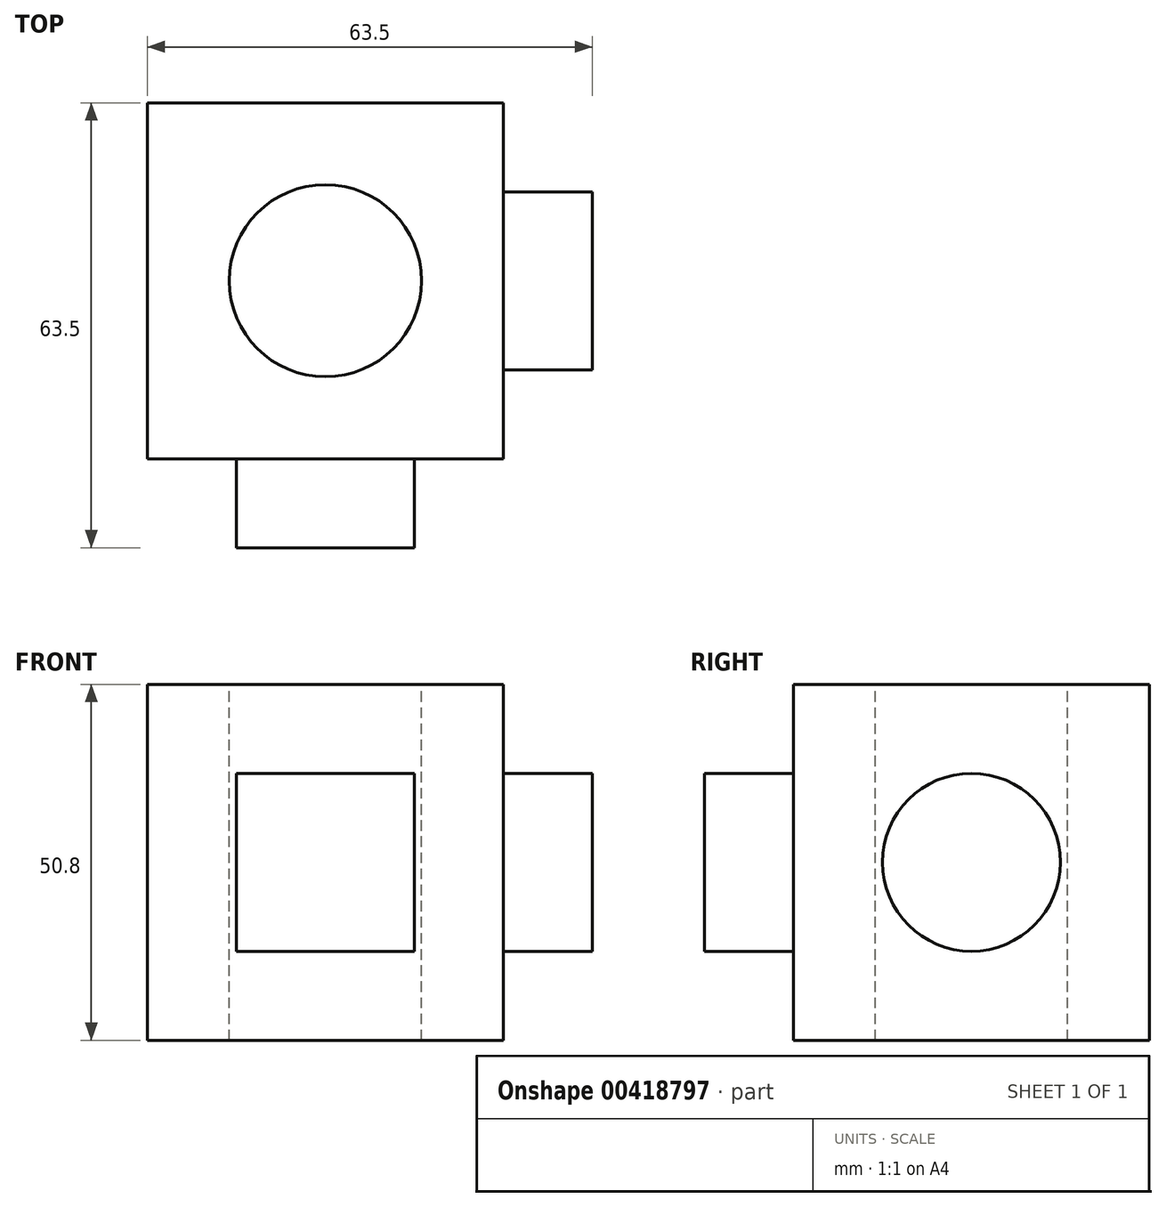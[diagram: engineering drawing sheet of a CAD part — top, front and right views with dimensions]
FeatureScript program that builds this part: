
annotation { "Feature Type Name" : "Feature", "Feature Type Description" : "" }
export const myFeature = defineFeature(function(context is Context, id is Id, definition is map)
    precondition{}
    {
        {
            var Q0;
            Q0=qCreatedBy(makeId("Front.planeOp"),FACE);
            var sketch = newSketch(context, id + "F0", { "sketchPlane" : qUnion([Q0])});
            skLineSegment(sketch, "E0.bottom", {"start": v(0, 0) * mm, "end": v(50.8, 0) * mm});
            skLineSegment(sketch, "E0.top", {"start": v(0, 50.8) * mm, "end": v(50.8, 50.8) * mm});
            skLineSegment(sketch, "E0.left", {"start": v(0, 0) * mm, "end": v(0, 50.8) * mm});
            skLineSegment(sketch, "E0.right", {"start": v(50.8, 0) * mm, "end": v(50.8, 50.8) * mm});
            skSolve(sketch);
        }
        {
            var Q0;
            Q0 = qSketchRegion(id + "F0", true);
            extrude(context, id + "F1", {"entities" : qUnion([Q0]), "depth" : 50.8 * mm});
        }
        {
            var Q0;
            Q0=makeQuery(id+"F1.opExtrude","SWEPT_FACE",FACE,{"disambiguationData":[OSD([sQuery(id+"F0.wireOp",EDGE,"E0.top")])]});
            var sketch = newSketch(context, id + "F2", { "sketchPlane" : qUnion([Q0])});
            skCircle(sketch, "E1", {"center": v(25.4, -25.4) * mm, "radius": 13.71 * mm});
            skSolve(sketch);
        }
        {
            var Q0;
            Q0=makeQuery(id+"F2.imprint","IMPRINT",FACE,{"disambiguationData":[TD([[makeQuery(id+"F2.imprint","IMPRINT",EDGE,{"derivedFrom":sQuery(id+"F2.wireOp",EDGE,"E1")}),1.0]])]});
            extrude(context, id + "F3", {"entities" : qUnion([Q0]), "operationType" : NewBodyOperationType.REMOVE, "oppositeDirection" : true, "depth" : 50.8 * mm});
        }
        {
            var Q0;
            Q0=makeQuery(id+"F1.opExtrude","CAP_FACE",FACE,{"disambiguationData":[OSD([sQuery(id+"F0.wireOp",EDGE,"E0.bottom"),sQuery(id+"F0.wireOp",EDGE,"E0.top"),sQuery(id+"F0.wireOp",EDGE,"E0.left"),sQuery(id+"F0.wireOp",EDGE,"E0.right")])],"isStart":false});
            var sketch = newSketch(context, id + "F4", { "sketchPlane" : qUnion([Q0])});
            skLineSegment(sketch, "E2.bottom", {"start": v(12.7, 38.1) * mm, "end": v(38.1, 38.1) * mm});
            skLineSegment(sketch, "E2.top", {"start": v(12.7, 12.7) * mm, "end": v(38.1, 12.7) * mm});
            skLineSegment(sketch, "E2.left", {"start": v(12.7, 38.1) * mm, "end": v(12.7, 12.7) * mm});
            skLineSegment(sketch, "E2.right", {"start": v(38.1, 38.1) * mm, "end": v(38.1, 12.7) * mm});
            skSolve(sketch);
        }
        {
            var Q0;
            Q0=makeQuery(id+"F4.imprint","IMPRINT",FACE,{"disambiguationData":[TD([[makeQuery(id+"F4.imprint","IMPRINT",EDGE,{"derivedFrom":sQuery(id+"F4.wireOp",EDGE,"E2.bottom")}),-1.0]])]});
            extrude(context, id + "F5", {"entities" : qUnion([Q0]), "operationType" : NewBodyOperationType.ADD, "depth" : 12.7 * mm});
        }
        {
            var Q0;
            Q0=makeQuery(id+"F1.opExtrude","SWEPT_FACE",FACE,{"disambiguationData":[OSD([sQuery(id+"F0.wireOp",EDGE,"E0.right")])]});
            var sketch = newSketch(context, id + "F6", { "sketchPlane" : qUnion([Q0])});
            skCircle(sketch, "E3", {"center": v(-25.4, 25.4) * mm, "radius": 12.7 * mm});
            skSolve(sketch);
        }
        {
            var Q0;
            Q0=makeQuery(id+"F6.imprint","IMPRINT",FACE,{"disambiguationData":[TD([[makeQuery(id+"F6.imprint","IMPRINT",EDGE,{"derivedFrom":sQuery(id+"F6.wireOp",EDGE,"E3")}),1.0]])]});
            extrude(context, id + "F7", {"entities" : qUnion([Q0]), "operationType" : NewBodyOperationType.ADD, "depth" : 12.7 * mm});
        }
    });
